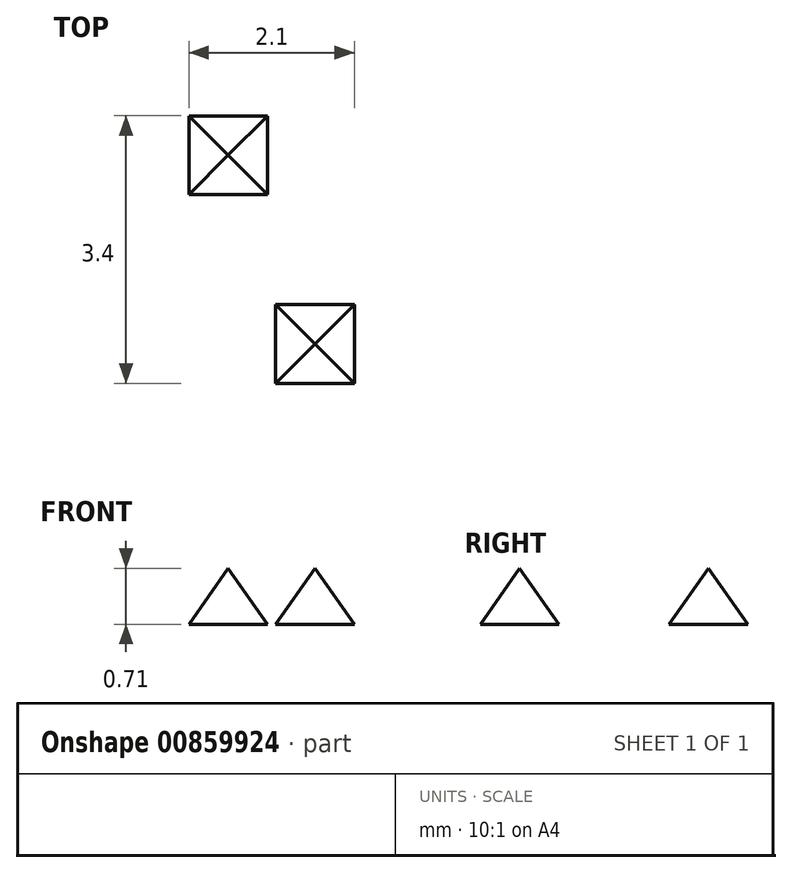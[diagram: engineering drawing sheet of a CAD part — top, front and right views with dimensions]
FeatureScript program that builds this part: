
annotation { "Feature Type Name" : "Feature", "Feature Type Description" : "" }
export const myFeature = defineFeature(function(context is Context, id is Id, definition is map)
    precondition{}
    {
        {
            var Q0;
            Q0=qCreatedBy(makeId("Top.planeOp"),FACE);
            var sketch = newSketch(context, id + "F0", { "sketchPlane" : qUnion([Q0])});
            skLineSegment(sketch, "E0.bottom", {"start": v(-0.5, 0.5) * mm, "end": v(0.5, 0.5) * mm});
            skLineSegment(sketch, "E0.top", {"start": v(-0.5, -0.5) * mm, "end": v(0.5, -0.5) * mm});
            skLineSegment(sketch, "E0.left", {"start": v(-0.5, 0.5) * mm, "end": v(-0.5, -0.5) * mm});
            skLineSegment(sketch, "E0.right", {"start": v(0.5, 0.5) * mm, "end": v(0.5, -0.5) * mm});
            skPoint(sketch, "E0.middle", {"position": v(0, 0) * mm});
            skCircle(sketch, "E1", {"center": v(0, 0) * mm, "radius": 0.7 * mm, "construction": true});
            skSolve(sketch);
        }
        {
            var Q0;
            Q0=qCreatedBy(makeId("Right.planeOp"),FACE);
            var sketch = newSketch(context, id + "F1", { "sketchPlane" : qUnion([Q0])});
            skLineSegment(sketch, "E2.0", {"start": v(-0.7, 0) * mm, "end": v(0.7, 0) * mm, "construction": true});
            skCircle(sketch, "E3", {"center": v(0, 0) * mm, "radius": 0.7 * mm, "construction": true});
            skLineSegment(sketch, "E4", {"start": v(0, 0) * mm, "end": v(0, 0.7) * mm});
            skSolve(sketch);
        }
        {
            var Q0;
            Q0=sQuery(id+"F1.wireOp",EDGE,"E2.0");
            cPoint(context, id + "F2", {"entities" : qUnion([Q0]), "parameter" : 0.5});
        }
        {
            var Q0;
            Q0=sQuery(id+"F1.wireOp",VERTEX,"E4.end");
            var Q1;
            Q1 = qCreatedBy(id + "F2" ,VERTEX);
            var Q2;
            Q2=sQuery(id+"F0.wireOp",VERTEX,"E0.bottom.start");
            cPlane(context, id + "F3", {"entities" : qUnion([Q0, Q1, Q2]), "cplaneType" : CPlaneType.THREE_POINT, "offset" : 25 * mm, "width" : 150 * mm, "height" : 150 * mm});
        }
        {
            var Q0;
            Q0=qCreatedBy(id+"F3.planeOp",FACE);
            var sketch = newSketch(context, id + "F4", { "sketchPlane" : qUnion([Q0])});
            skPoint(sketch, "E5.0", {"position": v(-0.7, 0) * mm});
            skPoint(sketch, "E6.0", {"position": v(0, 0.7) * mm});
            skLineSegment(sketch, "E7", {"start": v(-0.7, 0) * mm, "end": v(0, 0.7) * mm});
            skLineSegment(sketch, "E8", {"start": v(0, 0) * mm, "end": v(-0.7, 0) * mm, "construction": true});
            skPoint(sketch, "E9.0", {"position": v(0.7, 0) * mm});
            skLineSegment(sketch, "E10", {"start": v(0, 0.7) * mm, "end": v(0.7, 0) * mm});
            skLineSegment(sketch, "E11", {"start": v(0, 0) * mm, "end": v(0.7, 0) * mm, "construction": true});
            skSolve(sketch);
        }
        {
            var Q0;
            Q0=sQuery(id+"F0.wireOp",VERTEX,"E0.bottom.end");
            var Q1;
            Q1=sQuery(id+"F4.wireOp",VERTEX,"E6.0");
            var Q2;
            Q2=sQuery(id+"F0.wireOp",VERTEX,"E0.top.start");
            cPlane(context, id + "F5", {"entities" : qUnion([Q0, Q1, Q2]), "cplaneType" : CPlaneType.THREE_POINT, "offset" : 25 * mm, "width" : 150 * mm, "height" : 150 * mm});
        }
        {
            var Q0;
            Q0=makeQuery(id+"F0.imprint","IMPRINT",FACE,{"disambiguationData":[TD([[makeQuery(id+"F0.imprint","IMPRINT",EDGE,{"derivedFrom":sQuery(id+"F0.wireOp",EDGE,"E0.bottom")}),-1.0]])]});
            var Q1;
            Q1=sQuery(id+"F4.wireOp",VERTEX,"E6.0");
            loft(context, id + "F6", {"sheetProfilesArray" : [{ "sheetProfileEntities" : qUnion([Q0]) }, { "sheetProfileEntities" : qUnion([Q1]) }]});
        }
        {
            var Q0;
            Q0=qCreatedBy(makeId("Top.planeOp"),FACE);
            var sketch = newSketch(context, id + "F7", { "sketchPlane" : qUnion([Q0])});
            skLineSegment(sketch, "E12.bottom", {"start": v(-1.6, 1.9) * mm, "end": v(-0.6, 1.9) * mm});
            skLineSegment(sketch, "E12.top", {"start": v(-1.6, 2.9) * mm, "end": v(-0.6, 2.9) * mm});
            skLineSegment(sketch, "E12.left", {"start": v(-1.6, 1.9) * mm, "end": v(-1.6, 2.9) * mm});
            skLineSegment(sketch, "E12.right", {"start": v(-0.6, 1.9) * mm, "end": v(-0.6, 2.9) * mm});
            skPoint(sketch, "E12.middle", {"position": v(-1.1, 2.4) * mm});
            skLineSegment(sketch, "E13", {"start": v(-0.6, 1.9) * mm, "end": v(-1.6, 2.9) * mm, "construction": true});
            skSolve(sketch);
        }
        {
            var Q0;
            Q0=sQuery(id+"F7.wireOp",EDGE,"E13");
            cPlane(context, id + "F8", {"entities" : qUnion([Q0]), "cplaneType" : CPlaneType.LINE_ANGLE, "offset" : 25 * mm, "angle" : 90 * degree, "width" : 150 * mm, "height" : 150 * mm});
        }
        {
            var Q0;
            Q0=qCreatedBy(id+"F8.planeOp",FACE);
            var sketch = newSketch(context, id + "F9", { "sketchPlane" : qUnion([Q0])});
            skPoint(sketch, "E14.0", {"position": v(2.48, 0) * mm});
            skLineSegment(sketch, "E15", {"start": v(2.48, 0) * mm, "end": v(2.48, 0.7) * mm});
            skPoint(sketch, "E16.0", {"position": v(3.18, 0) * mm});
            skLineSegment(sketch, "E17", {"start": v(3.18, 0) * mm, "end": v(2.48, 0.7) * mm, "construction": true});
            skSolve(sketch);
        }
        {
            var Q0;
            Q0=makeQuery(id+"F7.imprint","IMPRINT",FACE,{"disambiguationData":[TD([[makeQuery(id+"F7.imprint","IMPRINT",EDGE,{"derivedFrom":sQuery(id+"F7.wireOp",EDGE,"E12.bottom")}),1.0]])]});
            var Q1;
            Q1=sQuery(id+"F9.wireOp",VERTEX,"E15.end");
            loft(context, id + "F10", {"sheetProfilesArray" : [{ "sheetProfileEntities" : qUnion([Q0]) }, { "sheetProfileEntities" : qUnion([Q1]) }]});
        }
    });
